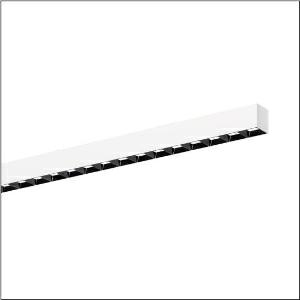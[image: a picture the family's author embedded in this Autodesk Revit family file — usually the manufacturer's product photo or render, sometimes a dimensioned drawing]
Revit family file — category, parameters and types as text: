
# Revit family: silica_21_51mx24tbt5w
name_source: partatom
category: Lighting Fixtures
units: mm (PartAtom-declared; Revit-internal decimal feet)

## family parameters
Cut with Voids When Loaded = No
Host = Face
Light Source = No
Part Type = Normal
Room Calculation Point = No
Round Connector Dimension = Use Diameter
Shared = No

## types (1)
- --- (1 x LED, 4100 lm, 40.5 W, 6500K)
    Apparent Load = 41 VA
    CIE Flux Codes = 74 94 99 100 100
    Color Rendering = 80
    Color Temperature = 6500K
    Default Elevation = 1800 mm
    Description = Silica 21, office luminaire, primary light control with darklight reflector, of PMMA, black, light emission: direct distribution, primary light characteristic: asymmetric, installation type: surface-mounted, LED, rated luminous flux: 4.100lm, luminous efficacy: 96lm/W, light colour: 8tw, colour temperature: 2700..6500K, control gear: DALI DT8, with terminal, 3+2-pole, max. 2.5mm², mains connection: 220..240V, AC, 50/60Hz, rated input power: 42.6W, luminaire housing, of aluminium, traffic white (RAL 9016), length: 1.504mm, width: 53mm, height: 53mm, protection rating (complete): IP20, insulation class (complete): insulation class I (protective earthing), certification: CE, permissible operating ambient temperature: 0..+35°C, standard: EN 50419, packaging unit: 1 piece
    Height = 53 mm
    Lamp = 1 x LED
    Lamp Light Flux = 4100 lm
    Lamp Power = 40.5 W
    Lamp count = 1
    Length = 1504 mm
    Luminous efficacy = 101 lm/W
    Manufacturer = Siteco
    ModVariant = No
    Model = 51MX24TBT5W
    Mounting Place = Ceiling
    Mounting Type = Surface mounted
    Number of Poles = 1
    OnlyDefault = Yes
    Power Factor = 1
    Product Name = Silica 21
    Product group = office luminaire | ceiling mounted
    ProductGroupID = 301
    Protection Class = Protection class I
    Protection Degree = IP 20
    RLX_Detail_Level = 1
    RLX_Emergency_Light_Flux = 0 lm
    RLX_Emergency_Type = 0
    RLX_Emergency_Type_DB = No
    RlxData = <blob elided: 41837 chars, md5=3eabdc75>
    Socket = socket
    Standby Power = 0 W
    System Light Flux = 4100 lm
    System Power = 41 W
    Type Comments = individual setting
    Type Image = l_1335873.jpg
    URL = http://relux.com
    VarID = @adj_141061
    Voltage = 0 V
    Weight = 0.00 kg
    Width = 53 mm

## geometry (parser evidence)
native form markers: Blend x4, Sweep x10
no freeform markers — native parametric forms only
